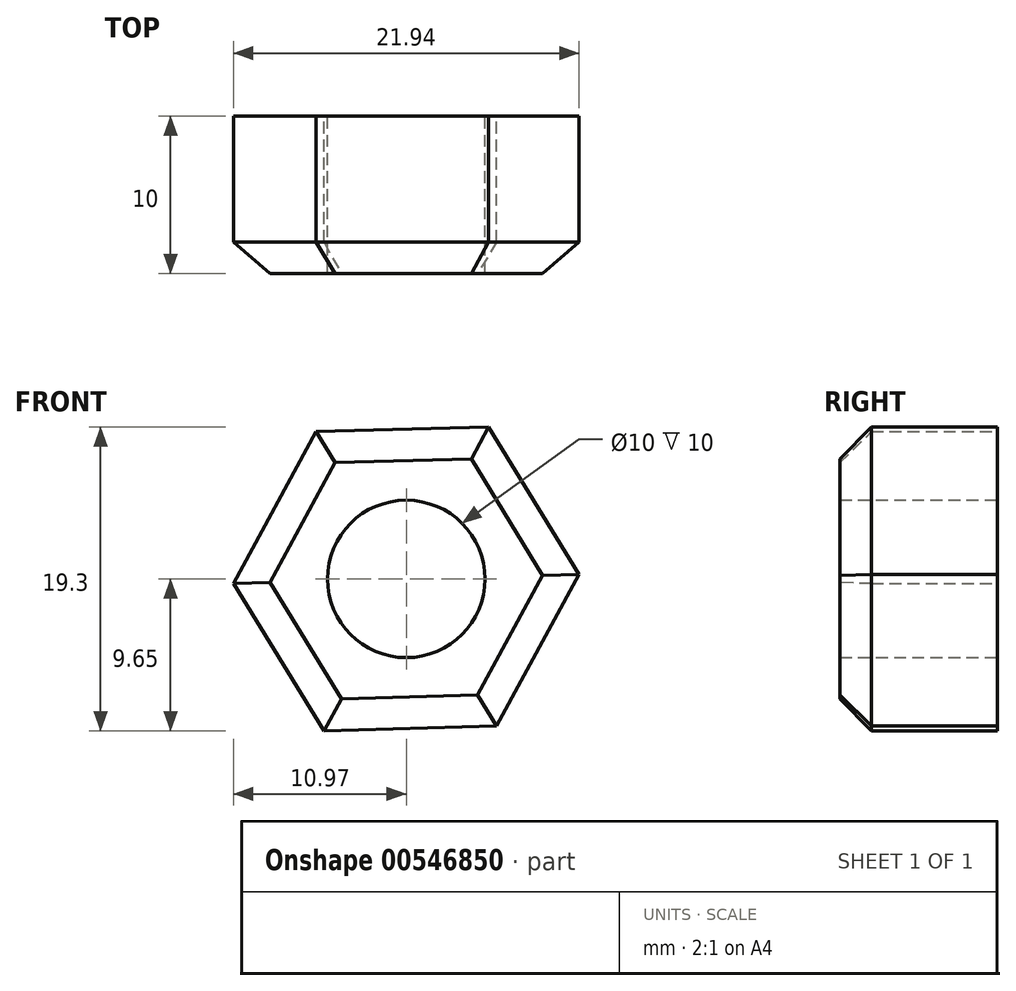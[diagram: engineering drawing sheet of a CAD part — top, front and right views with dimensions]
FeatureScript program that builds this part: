
annotation { "Feature Type Name" : "Feature", "Feature Type Description" : "" }
export const myFeature = defineFeature(function(context is Context, id is Id, definition is map)
    precondition{}
    {
        {
            var Q0;
            Q0=qCreatedBy(makeId("Front.planeOp"),FACE);
            var sketch = newSketch(context, id + "F0", { "sketchPlane" : qUnion([Q0])});
            skCircle(sketch, "E0", {"center": v(0, 0) * mm, "radius": 5 * mm});
            skCircle(sketch, "E1.cCircle", {"center": v(0, 0) * mm, "radius": 9.5 * mm, "construction": true});
            skLineSegment(sketch, "E1.0", {"start": v(-10.97, -0.3) * mm, "end": v(-5.74, 9.35) * mm});
            skLineSegment(sketch, "E1.1", {"start": v(-5.74, 9.35) * mm, "end": v(5.23, 9.65) * mm});
            skLineSegment(sketch, "E1.2", {"start": v(5.23, 9.65) * mm, "end": v(10.97, 0.3) * mm});
            skLineSegment(sketch, "E1.3", {"start": v(10.97, 0.3) * mm, "end": v(5.74, -9.35) * mm});
            skLineSegment(sketch, "E1.4", {"start": v(5.74, -9.35) * mm, "end": v(-5.23, -9.65) * mm});
            skLineSegment(sketch, "E1.5", {"start": v(-5.23, -9.65) * mm, "end": v(-10.97, -0.3) * mm});
            skPoint(sketch, "E1.0.midPoint", {"position": v(-8.36, 4.53) * mm});
            skSolve(sketch);
        }
        {
            var Q0;
            Q0=makeQuery(id+"F0.imprint","IMPRINT",FACE,{"disambiguationData":[TD([[makeQuery(id+"F0.imprint","IMPRINT",EDGE,{"derivedFrom":sQuery(id+"F0.wireOp",EDGE,"E0")}),-1.0]])]});
            extrude(context, id + "F1", {"entities" : qUnion([Q0]), "depth" : 10 * mm, "offsetDistance" : 25 * mm});
        }
        {
            var Q0;
            Q0=makeQuery(id+"F1.opExtrude","CAP_EDGE",EDGE,{"disambiguationData":[OSD([sQuery(id+"F0.wireOp",EDGE,"E1.2")])],"isStart":false});
            var Q1;
            Q1=makeQuery(id+"F1.opExtrude","CAP_EDGE",EDGE,{"disambiguationData":[OSD([sQuery(id+"F0.wireOp",EDGE,"E1.3")])],"isStart":false});
            var Q2;
            Q2=makeQuery(id+"F1.opExtrude","CAP_EDGE",EDGE,{"disambiguationData":[OSD([sQuery(id+"F0.wireOp",EDGE,"E1.4")])],"isStart":false});
            var Q3;
            Q3=makeQuery(id+"F1.opExtrude","CAP_EDGE",EDGE,{"disambiguationData":[OSD([sQuery(id+"F0.wireOp",EDGE,"E1.5")])],"isStart":false});
            var Q4;
            Q4=makeQuery(id+"F1.opExtrude","CAP_EDGE",EDGE,{"disambiguationData":[OSD([sQuery(id+"F0.wireOp",EDGE,"E1.0")])],"isStart":false});
            var Q5;
            Q5=makeQuery(id+"F1.opExtrude","CAP_EDGE",EDGE,{"disambiguationData":[OSD([sQuery(id+"F0.wireOp",EDGE,"E1.1")])],"isStart":false});
            chamfer(context, id + "F2", {"entities" : qUnion([Q0, Q1, Q2, Q3, Q4, Q5]), "width" : 2 * mm, "tangentPropagation" : true});
        }
    });
